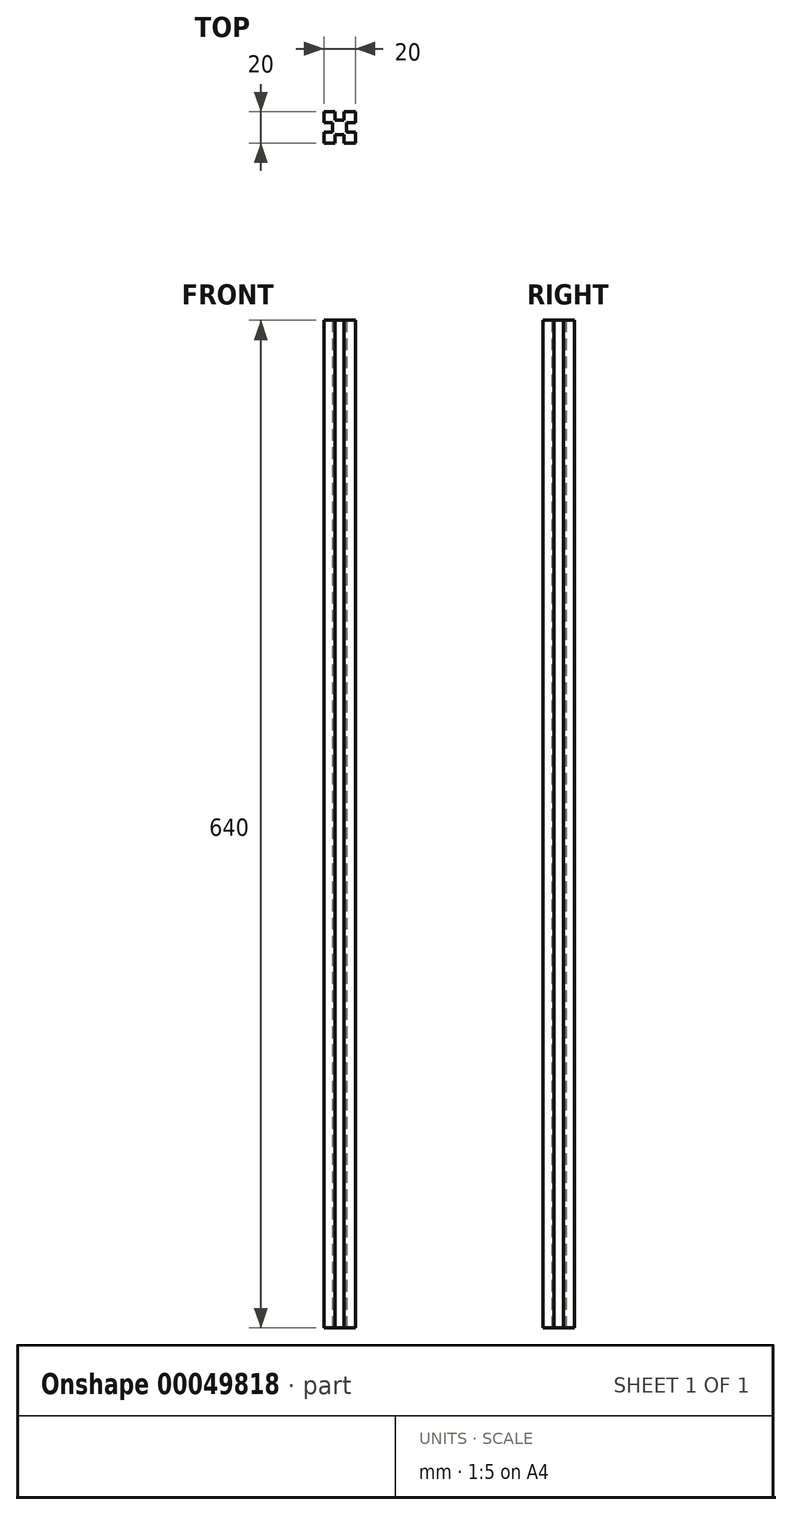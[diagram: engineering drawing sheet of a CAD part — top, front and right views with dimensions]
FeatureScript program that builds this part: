
annotation { "Feature Type Name" : "Feature", "Feature Type Description" : "" }
export const myFeature = defineFeature(function(context is Context, id is Id, definition is map)
    precondition{}
    {
        {
            var Q0;
            Q0=qCreatedBy(makeId("Top.planeOp"),FACE);
            var sketch = newSketch(context, id + "F0", { "sketchPlane" : qUnion([Q0])});
            skLineSegment(sketch, "E0.bottom", {"start": v(0, 0) * mm, "end": v(20, 0) * mm});
            skLineSegment(sketch, "E0.top", {"start": v(0, 20) * mm, "end": v(20, 20) * mm});
            skLineSegment(sketch, "E0.left", {"start": v(0, 0) * mm, "end": v(0, 20) * mm});
            skLineSegment(sketch, "E0.right", {"start": v(20, 0) * mm, "end": v(20, 20) * mm});
            skLineSegment(sketch, "E1.bottom", {"start": v(7, 20) * mm, "end": v(13, 20) * mm});
            skLineSegment(sketch, "E1.top", {"start": v(7, 14.5) * mm, "end": v(13, 14.5) * mm});
            skLineSegment(sketch, "E1.left", {"start": v(7, 20) * mm, "end": v(7, 14.5) * mm});
            skLineSegment(sketch, "E1.right", {"start": v(13, 20) * mm, "end": v(13, 14.5) * mm});
            skLineSegment(sketch, "E2.bottom", {"start": v(20, 13) * mm, "end": v(14.5, 13) * mm});
            skLineSegment(sketch, "E2.top", {"start": v(20, 7) * mm, "end": v(14.5, 7) * mm});
            skLineSegment(sketch, "E2.left", {"start": v(20, 13) * mm, "end": v(20, 7) * mm});
            skLineSegment(sketch, "E2.right", {"start": v(14.5, 13) * mm, "end": v(14.5, 7) * mm});
            skLineSegment(sketch, "E3.bottom", {"start": v(13, 0) * mm, "end": v(7, 0) * mm});
            skLineSegment(sketch, "E3.top", {"start": v(13, 5.5) * mm, "end": v(7, 5.5) * mm});
            skLineSegment(sketch, "E3.left", {"start": v(13, 0) * mm, "end": v(13, 5.5) * mm});
            skLineSegment(sketch, "E3.right", {"start": v(7, 0) * mm, "end": v(7, 5.5) * mm});
            skLineSegment(sketch, "E4.bottom", {"start": v(0, 7) * mm, "end": v(5.5, 7) * mm});
            skLineSegment(sketch, "E4.top", {"start": v(0, 13) * mm, "end": v(5.5, 13) * mm});
            skLineSegment(sketch, "E4.left", {"start": v(0, 7) * mm, "end": v(0, 13) * mm});
            skLineSegment(sketch, "E4.right", {"start": v(5.5, 7) * mm, "end": v(5.5, 13) * mm});
            skSolve(sketch);
        }
        {
            var Q0;
            Q0=makeQuery(id+"F0.imprint","IMPRINT",FACE,{"disambiguationData":[TD([[makeQuery(id+"F0.imprint","IMPRINT",EDGE,{"derivedFrom":sQuery(id+"F0.wireOp",EDGE,"E1.top")}),-1.0]])]});
            extrude(context, id + "F1", {"entities" : qUnion([Q0]), "depth" : 640 * mm});
        }
    });
